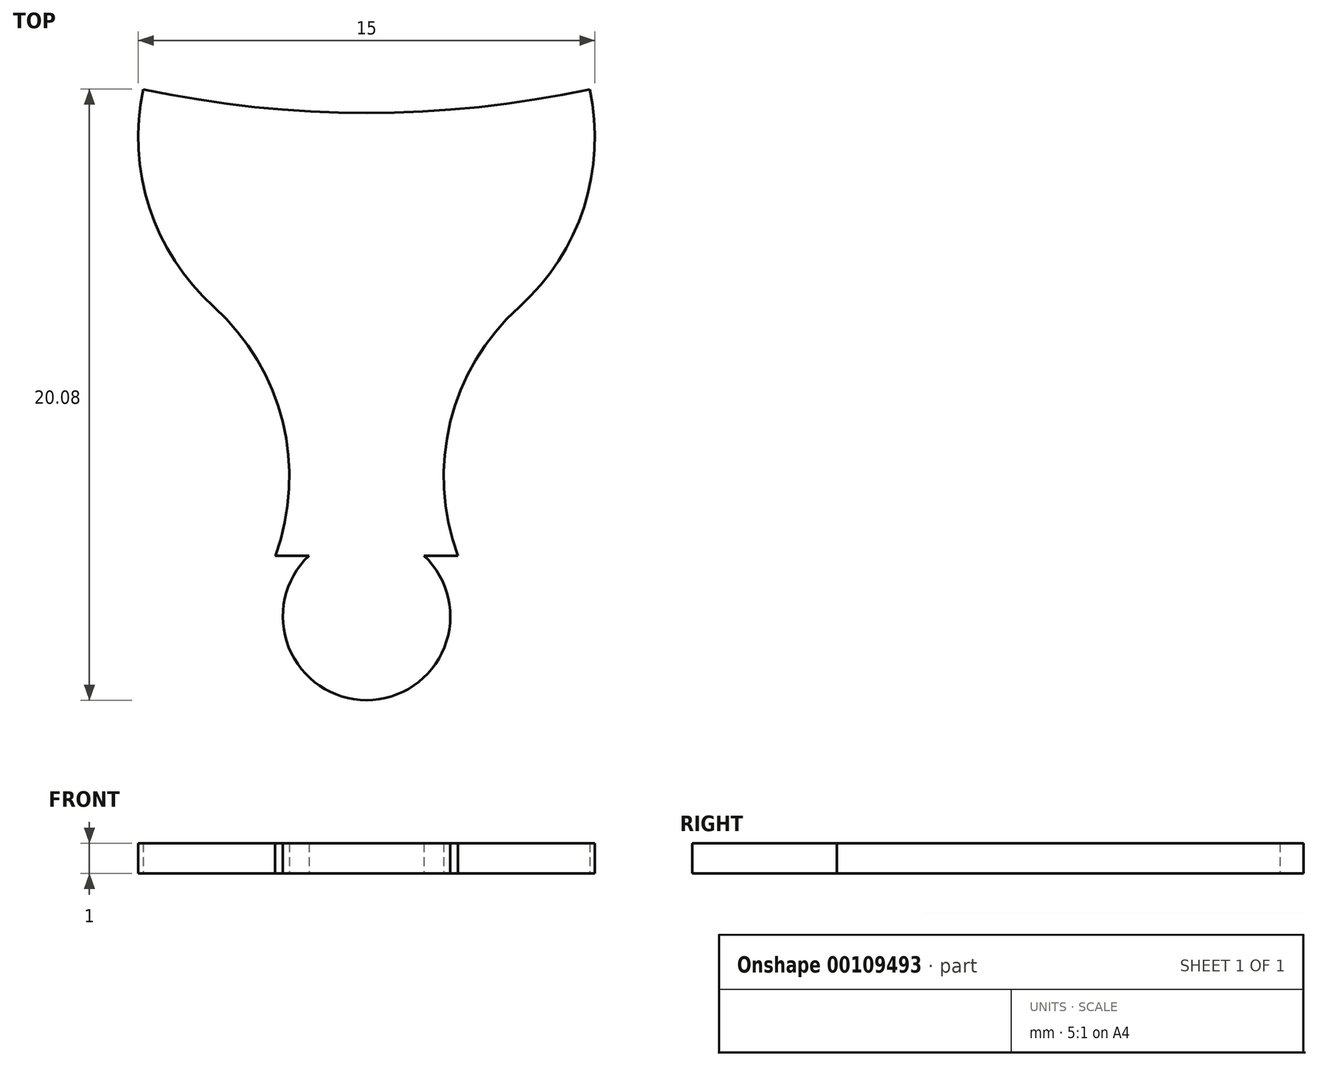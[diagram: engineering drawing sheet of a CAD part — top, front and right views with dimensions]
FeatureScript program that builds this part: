
annotation { "Feature Type Name" : "Feature", "Feature Type Description" : "" }
export const myFeature = defineFeature(function(context is Context, id is Id, definition is map)
    precondition{}
    {
        {
            var Q0;
            Q0=qCreatedBy(makeId("Top.planeOp"),FACE);
            var sketch = newSketch(context, id + "F0", { "sketchPlane" : qUnion([Q0])});
            skCircle(sketch, "E0", {"center": v(0, 0) * mm, "radius": 7.5 * mm});
            skLineSegment(sketch, "E1", {"start": v(0, 0) * mm, "end": v(0, -18.5) * mm});
            skLineSegment(sketch, "E2", {"start": v(0, 0) * mm, "end": v(-26.95, -26.95) * mm, "construction": true});
            skCircle(sketch, "E3", {"center": v(0, -15.75) * mm, "radius": 2.75 * mm});
            skLineSegment(sketch, "E4", {"start": v(-3, -13.75) * mm, "end": v(3, -13.75) * mm});
            skCircle(sketch, "E5", {"center": v(-10.03, -11.15) * mm, "radius": 7.5 * mm});
            skCircle(sketch, "E6", {"center": v(0, 35.8) * mm, "radius": 35 * mm});
            skLineSegment(sketch, "E7", {"start": v(0, 0) * mm, "end": v(0, 0.8) * mm});
            skSolve(sketch);
        }
        {
            var Q0;
            {var subQ0=sQuery(id+"F0.wireOp",EDGE,"E3");var subQ1=sQuery(id+"F0.wireOp",EDGE,"E1");var subQ2=makeQuery(id+"F0.imprint","INTERSECT",VERTEX,{"disambiguationData":[OD(0.0)],"derivedFrom":[subQ1,subQ0]});Q0=makeQuery(id+"F0.imprint","IMPRINT",FACE,{"disambiguationData":[TD([[makeQuery(id+"F0.imprint","IMPRINT",EDGE,{"disambiguationData":[TD([[subQ2,1.0]])],"derivedFrom":subQ1}),-1.0]])]});}
            var Q1;
            {var subQ0=sQuery(id+"F0.wireOp",EDGE,"E7");Q1=makeQuery(id+"F0.imprint","IMPRINT",FACE,{"disambiguationData":[TD([[makeQuery(id+"F0.imprint","IMPRINT",EDGE,{"derivedFrom":subQ0}),1.0]])]});}
            var Q2;
            {var subQ0=sQuery(id+"F0.wireOp",EDGE,"E5");var subQ6=sQuery(id+"F0.wireOp",EDGE,"E0");var subQ9=makeQuery(id+"F0.imprint","INTERSECT",VERTEX,{"derivedFrom":[subQ6,subQ0]});Q2=makeQuery(id+"F0.imprint","IMPRINT",FACE,{"disambiguationData":[TD([[makeQuery(id+"F0.imprint","IMPRINT",EDGE,{"disambiguationData":[TD([[subQ9,-1.0]])],"derivedFrom":subQ6}),-1.0]])]});}
            var Q3;
            {var subQ0=sQuery(id+"F0.wireOp",EDGE,"E3");var subQ1=sQuery(id+"F0.wireOp",EDGE,"E1");var subQ2=makeQuery(id+"F0.imprint","INTERSECT",VERTEX,{"disambiguationData":[OD(1.0)],"derivedFrom":[subQ1,subQ0]});Q3=makeQuery(id+"F0.imprint","IMPRINT",FACE,{"disambiguationData":[TD([[makeQuery(id+"F0.imprint","IMPRINT",EDGE,{"disambiguationData":[TD([[subQ2,-1.0]])],"derivedFrom":subQ1}),-1.0]])]});}
            extrude(context, id + "F1", {"entities" : qUnion([Q0, Q1, Q2, Q3]), "depth" : 1 * mm});
        }
        {
            var Q0;
            Q0=makeQuery(id+"F1.opExtrude","SWEPT_BODY",BODY,{"disambiguationData":[OSD([sQuery(id+"F0.wireOp",EDGE,"E0"),sQuery(id+"F0.wireOp",EDGE,"E1"),sQuery(id+"F0.wireOp",EDGE,"E3"),sQuery(id+"F0.wireOp",EDGE,"E4"),sQuery(id+"F0.wireOp",EDGE,"E5"),sQuery(id+"F0.wireOp",EDGE,"E6"),sQuery(id+"F0.wireOp",EDGE,"E7")])]});
            var Q1;
            Q1=qCreatedBy(makeId("Right.planeOp"),FACE);
            mirror(context, id + "F2", {"operationType" : NewBodyOperationType.ADD, "entities" : qUnion([Q0]), "mirrorPlane" : qUnion([Q1])});
        }
    });
